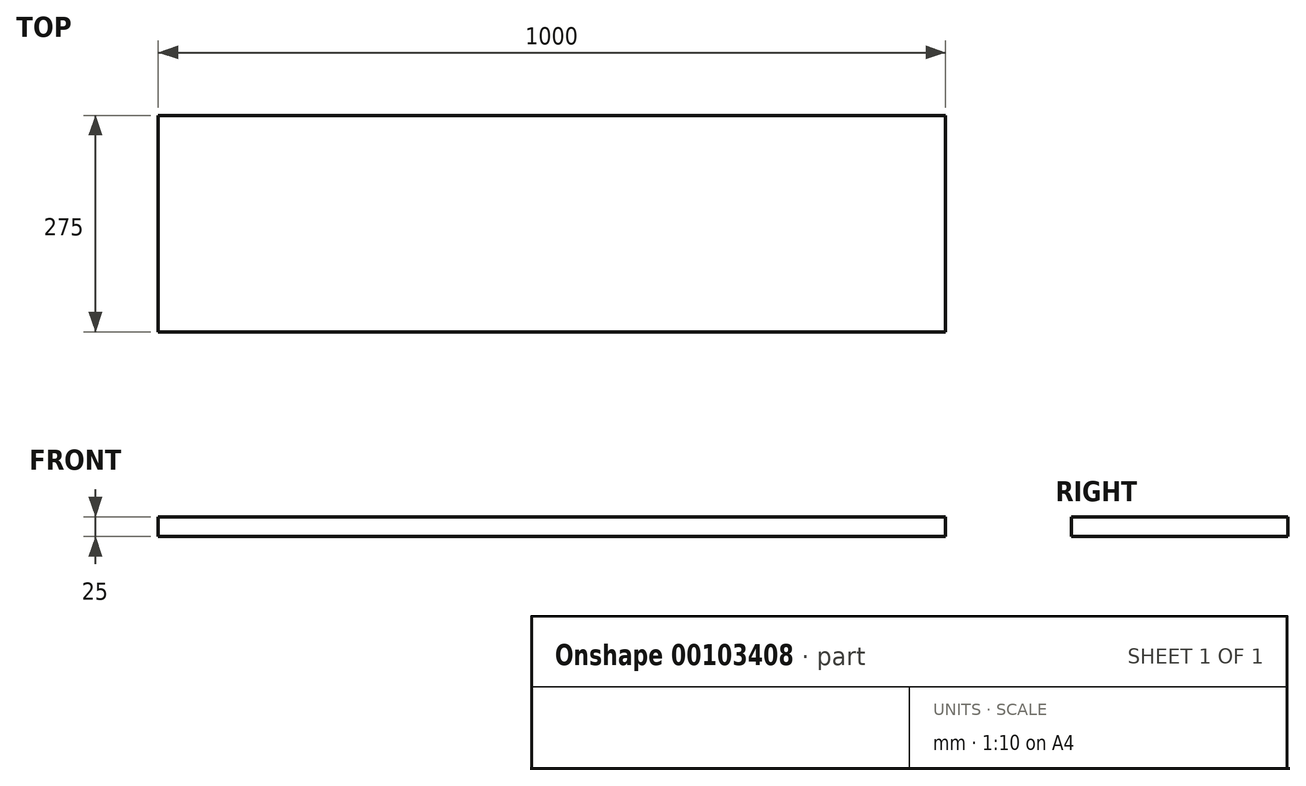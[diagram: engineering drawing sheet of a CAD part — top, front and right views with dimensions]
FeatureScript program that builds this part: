
annotation { "Feature Type Name" : "Feature", "Feature Type Description" : "" }
export const myFeature = defineFeature(function(context is Context, id is Id, definition is map)
    precondition{}
    {
        {
            var Q0;
            Q0=qCreatedBy(makeId("Top.planeOp"),FACE);
            var sketch = newSketch(context, id + "F0", { "sketchPlane" : qUnion([Q0])});
            skLineSegment(sketch, "E0.bottom", {"start": v(-500, 0) * mm, "end": v(500, 0) * mm});
            skLineSegment(sketch, "E0.top", {"start": v(-500, 275) * mm, "end": v(500, 275) * mm});
            skLineSegment(sketch, "E0.left", {"start": v(-500, 0) * mm, "end": v(-500, 275) * mm});
            skLineSegment(sketch, "E0.right", {"start": v(500, 0) * mm, "end": v(500, 275) * mm});
            skPoint(sketch, "E1", {"position": v(0, 0) * mm});
            skSolve(sketch);
        }
        {
            var Q0;
            Q0 = qSketchRegion(id + "F0", true);
            extrude(context, id + "F1", {"entities" : qUnion([Q0]), "depth" : 25 * mm, "offsetDistance" : 25 * mm});
        }
    });
